# Revit family: Loudspeaker_Fulcrum-Acoustic_GX15XX1
name_source: partatom
category: Communication Devices
revit_build: Autodesk Revit 2017 (Build: 20190508_0315(x64)
units: mm (PartAtom-declared; Revit-internal decimal feet)

## family parameters
Always vertical = No
Cut with Voids When Loaded = No
Maintain Annotation Orientation = No
OmniClass Number = 23.85.10.11.14.14.14
OmniClass Title = Loudspeakers
Part Type = Normal
Room Calculation Point = No
Round Connector Dimension = Use Diameter
Shared = No
Work Plane-Based = Yes

## types (4) — shared parameters
Connections = (2) Neutrik NL4 Speakon
Pin 1+/-: Full Range
Pin 2+/-: NC
Default Elevation = 48 "
Depth = 20 "
Description = GX15 – Dual 15” Coaxial Loudspeaker
Edition number = 1
Height = 30 "
Manufacturer = Fulcrum Acoustic
Mounting / Suspension Points = (12) M10 x 1.5 eye bolt angle points, (2) M10 x 1.5 yoke points,
(1) M10 x 1.5 pull back point
Net Weight = 61.00 lbf
Operating Mode = Single-amplified w/ DSP
Power Handling @ Nominal Impedance = 57 V / 400 W @ 8 Ω
Product Guid = 88a76114-8168-4e18-82cb-54654948be1e
Product data url = https://www.bimobject.com
Product url = https://www.fulcrum-acoustic.com
Recommended Power Amplifier = 400 W to 800 W @ 8 Ω
Shipping Weight = 71.00 lbf
Technical description = https://www.fulcrum-acoustic.com
Transducers = HF/LF: Coaxial 3.0” titanium diaphragm compression driver;
15.0” woofer, 3.0” voice coil; single ceramic magnet
URL = https://www.fulcrum-acoustic.com
Width = 21 "

## per-type parameters (varying)
| type | Equalized Maximum SPL (peak/continuous) | Equalized Sensitivity @ Input Voltage | Nominal Beamwidth | Nominal Maximum SPL (peak/continuous) | Nominal Sensitivity @ Input Voltage | Operating Range |
| GX1565 | 129 dB / 123 dB | 97 dB @ 2.83 V | 60° x 45° | 135 dB / 129 dB | 103 dB @ 2.83 V | 43 Hz to 18 kHz |
| GX1526 | 128 dB / 122 dB | 96 dB @ 2.83 V | 120° x 60° | 133 dB / 127 dB | 101 dB @ 2.83 V | 43 Hz to 20 kHz |
| GX1577 | 129 dB / 123 dB | 97 dB @ 2.83 V | 75° x 75° | 133 dB / 127 dB | 101 dB @ 2.83 V | 43 Hz to 19 kHz |
| GX1595 | 129 dB / 123 dB | 97 dB @ 2.83 V | 90° x 45° | 136 dB / 130 dB | 104 dB @ 2.83 V | 43 Hz to 19 kHz |

note: column(s) folded — value = type name in every type: Model

## geometry (parser evidence)
native form markers: Sweep x8
no freeform markers — native parametric forms only
